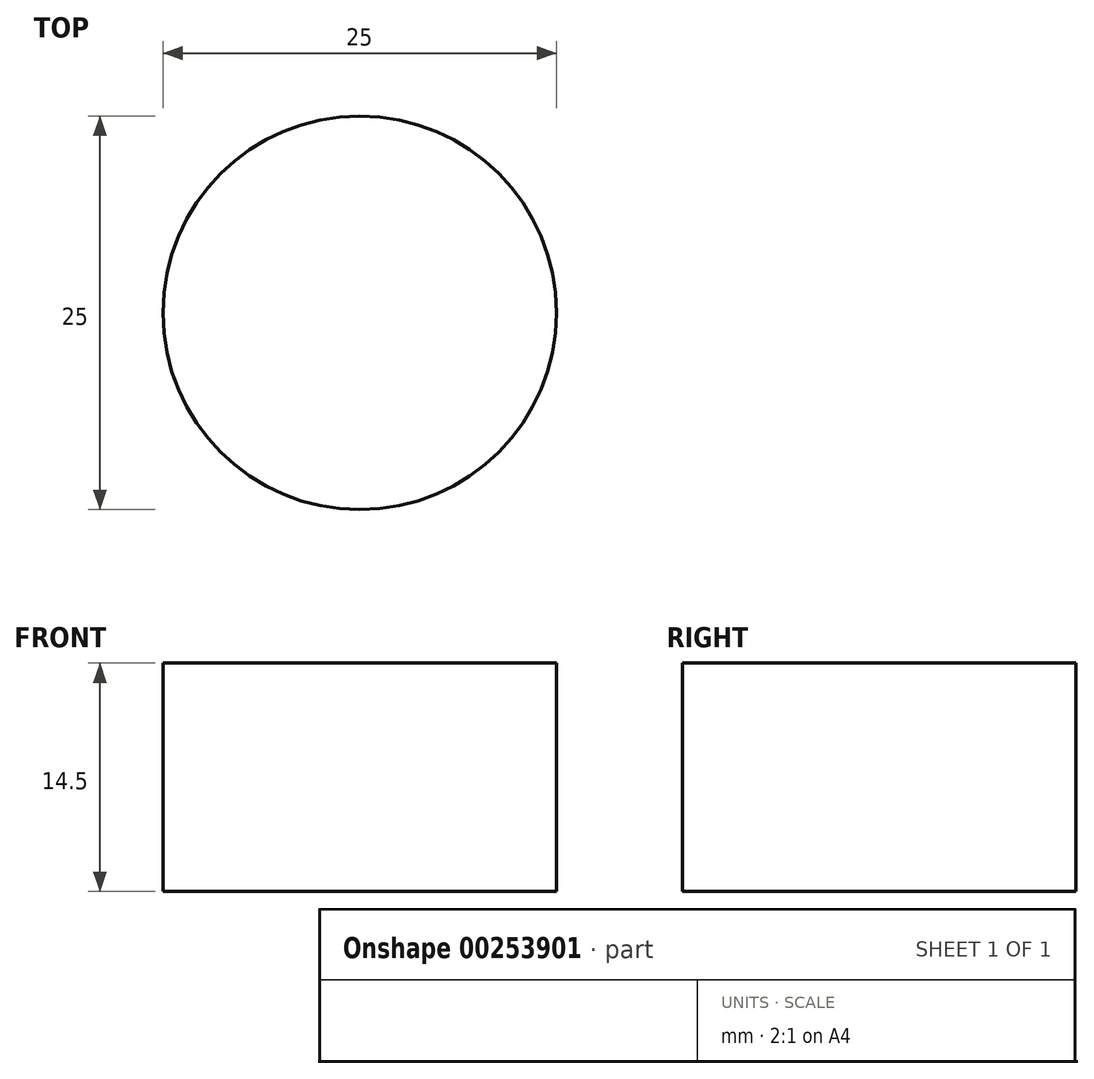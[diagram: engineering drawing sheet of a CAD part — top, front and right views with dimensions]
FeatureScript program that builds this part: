
annotation { "Feature Type Name" : "Feature", "Feature Type Description" : "" }
export const myFeature = defineFeature(function(context is Context, id is Id, definition is map)
    precondition{}
    {
        {
            var Q0;
            Q0=qCreatedBy(makeId("Top.planeOp"),FACE);
            var sketch = newSketch(context, id + "F0", { "sketchPlane" : qUnion([Q0])});
            skCircle(sketch, "E0", {"center": v(0, 0) * mm, "radius": 12.5 * mm});
            skSolve(sketch);
        }
        {
            var Q0;
            Q0 = qSketchRegion(id + "F0", true);
            extrude(context, id + "F1", {"entities" : qUnion([Q0]), "depth" : 14.5 * mm});
        }
    });
